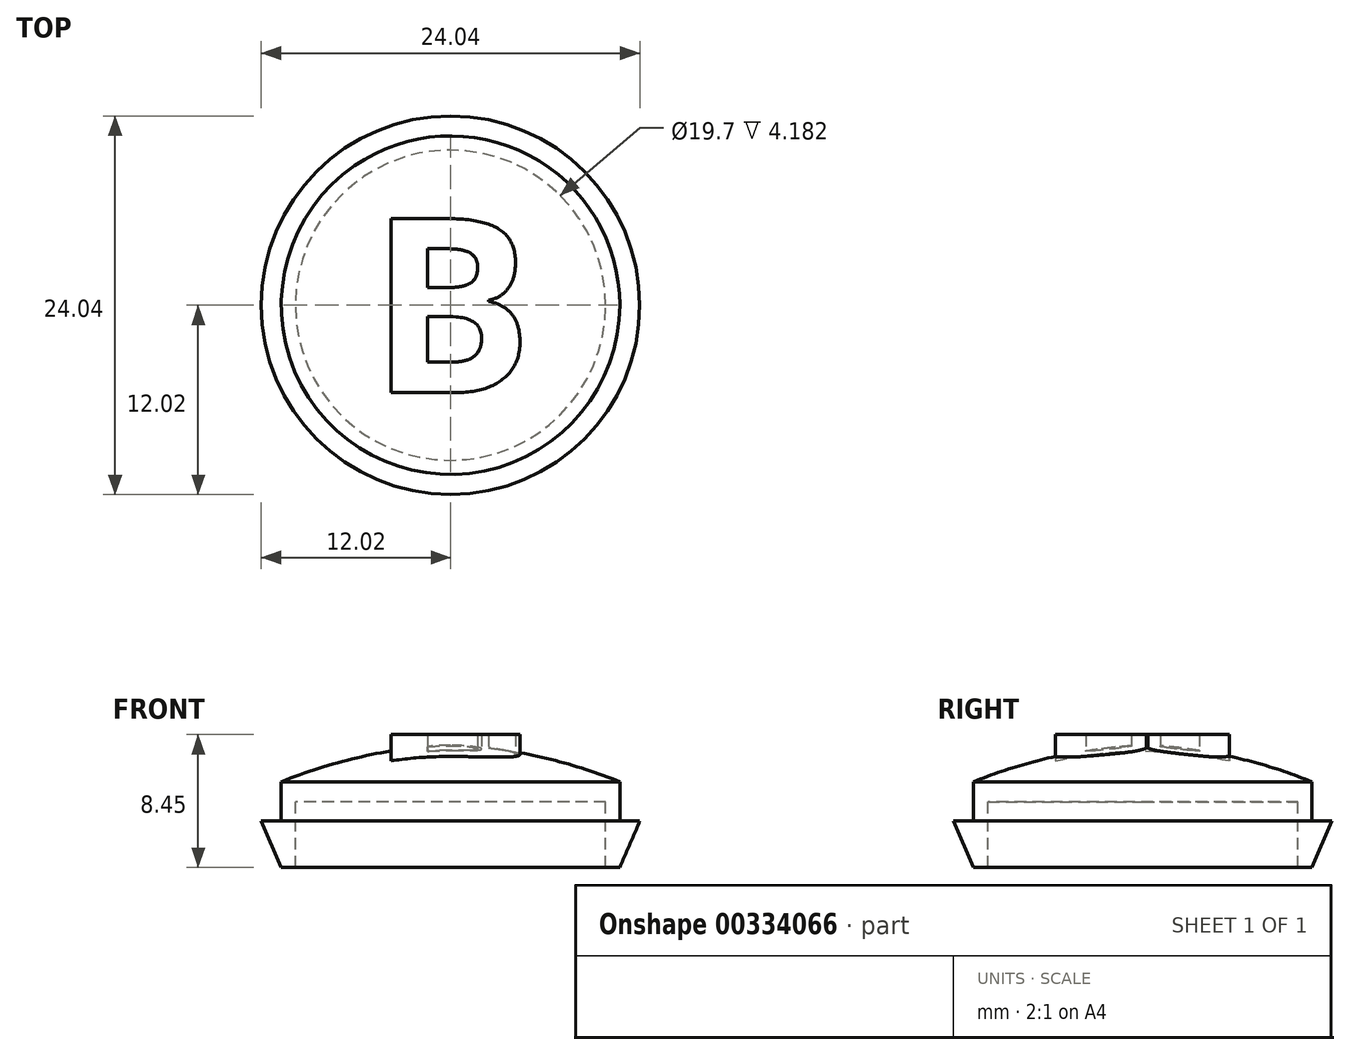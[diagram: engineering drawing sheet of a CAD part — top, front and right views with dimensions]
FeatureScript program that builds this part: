
annotation { "Feature Type Name" : "Feature", "Feature Type Description" : "" }
export const myFeature = defineFeature(function(context is Context, id is Id, definition is map)
    precondition{}
    {
        {
            var Q0;
            Q0=qCreatedBy(makeId("Front.planeOp"),FACE);
            var sketch = newSketch(context, id + "F0", { "sketchPlane" : qUnion([Q0])});
            skLineSegment(sketch, "E0", {"start": v(0, 0) * mm, "end": v(10.75, 0) * mm});
            skLineSegment(sketch, "E1", {"start": v(10.75, 0) * mm, "end": v(10.75, -2.5) * mm});
            skLineSegment(sketch, "E2", {"start": v(10.75, -2.5) * mm, "end": v(12.02, -2.5) * mm});
            skLineSegment(sketch, "E3", {"start": v(12.02, -2.5) * mm, "end": v(10.75, -5.45) * mm});
            skLineSegment(sketch, "E4", {"start": v(10.75, -5.45) * mm, "end": v(9.85, -5.45) * mm});
            skLineSegment(sketch, "E5", {"start": v(9.85, -5.45) * mm, "end": v(9.85, -1.27) * mm});
            skLineSegment(sketch, "E6", {"start": v(9.85, -1.27) * mm, "end": v(0, -1.27) * mm});
            skArc(sketch, "E7", {"start": v(10.75, 0) * mm, "mid": v(5.47, 1.63) * mm, "end": v(0, 2.37) * mm});
            skLineSegment(sketch, "E8", {"start": v(0, 2.37) * mm, "end": v(0, -1.27) * mm});
            skSolve(sketch);
        }
        {
            var Q0;
            {var subQ0=sQuery(id+"F0.wireOp",EDGE,"E0");Q0=makeQuery(id+"F0.imprint","IMPRINT",FACE,{"disambiguationData":[TD([[makeQuery(id+"F0.imprint","IMPRINT",EDGE,{"derivedFrom":subQ0}),1.0]])]});}
            var Q1;
            {var subQ0=sQuery(id+"F0.wireOp",EDGE,"E0");Q1=makeQuery(id+"F0.imprint","IMPRINT",FACE,{"disambiguationData":[TD([[makeQuery(id+"F0.imprint","IMPRINT",EDGE,{"derivedFrom":subQ0}),-1.0]])]});}
            var Q2;
            Q2=sQuery(id+"F0.wireOp",EDGE,"E8");
            revolve(context, id + "F1", {"entities" : qUnion([Q0, Q1]), "axis" : qUnion([Q2]), "revolveType" : RevolveType.FULL});
        }
        {
            var Q0;
            Q0=qCreatedBy(makeId("Top.planeOp"),FACE);
            var sketch = newSketch(context, id + "F2", { "sketchPlane" : qUnion([Q0])});
            skText(sketch, "E9", { "text": "B", "fontName": "OpenSans-Bold.ttf"});
            const initialGuessF2  = {"E9": [-0.00518, -0.00555, 1, 0, 0.01115]};
            skSetInitialGuess(sketch, initialGuessF2);
            skSolve(sketch);
        }
        {
            var Q0;
            Q0 = qSketchRegion(id + "F2", true);
            var Q1;
            Q1 = qConstructionFilter(qBodyType(qCreatedBy(id + "F2" ,EDGE), BodyType.WIRE), ConstructionObject.NO);
            extrude(context, id + "F3", {"entities" : qUnion([Q0]), "operationType" : NewBodyOperationType.ADD, "surfaceEntities" : qUnion([Q1]), "depth" : 3 * mm});
        }
    });
